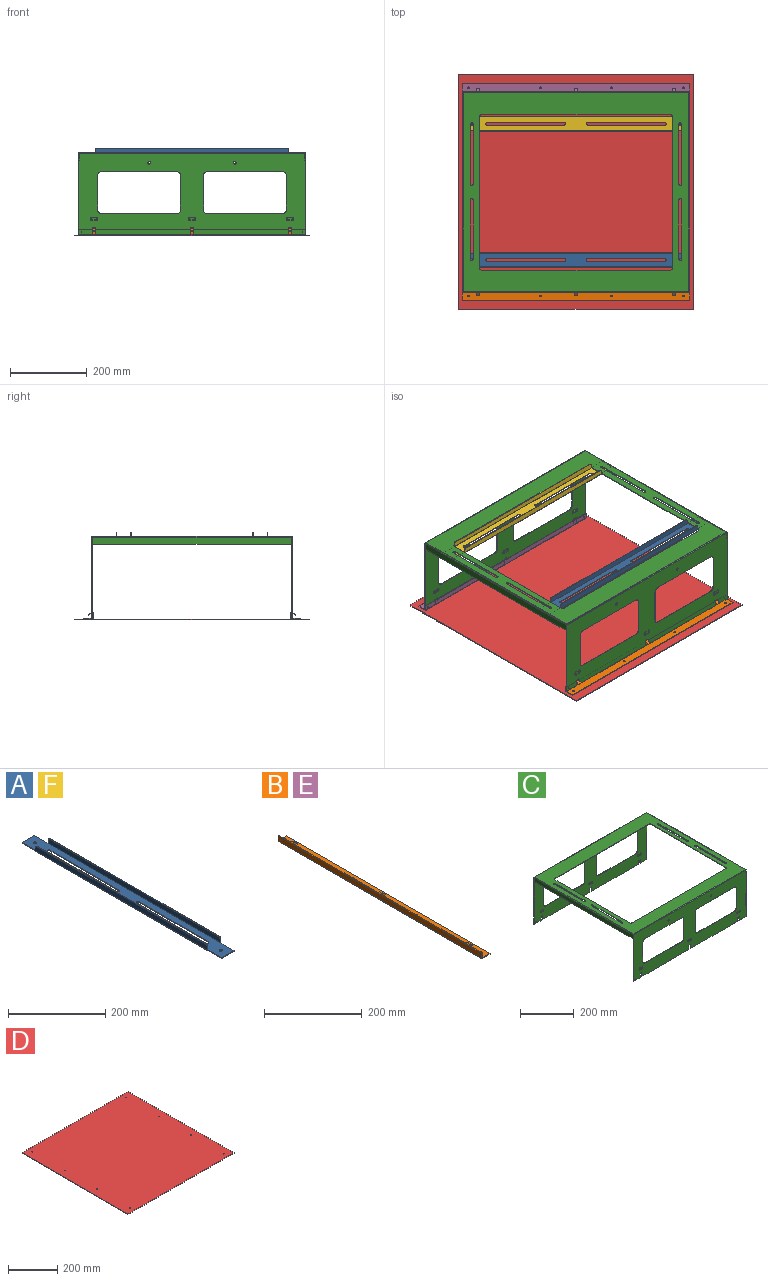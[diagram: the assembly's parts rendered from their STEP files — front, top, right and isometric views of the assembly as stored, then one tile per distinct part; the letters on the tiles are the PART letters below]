
ASSEMBLY  parts=6 mates=5
PART A: 40 faces, bbox 40x582x15 mm
  f0: plane 40x2mm, normal (-1,0,0), area 80mm2, adj f4,f16,f17,f36
  f1: plane 40x2mm, normal (1,0,0), area 80mm2, adj f2,f16,f17,f25
  f2: plane 35.8x2mm, normal (0,1,0), area 71.6mm2, adj f1,f15,f16,f17
  f3: plane 40x2mm, normal (1,0,0), area 80mm2, adj f4,f16,f17,f26
  f4: plane 35.8x2mm, normal (0,-1,0), area 71.6mm2, adj f0,f3,f16,f17
  f5: plane 200.9x2mm, normal (-1,0,0), area 401.8mm2, adj f6,f14,f16,f17
  f6: cylinder r=3.5mm len=7mm, axis (0,0,1), area 22.5mm2, adj f5,f7,f16,f17
  f7: plane 200.85x2mm, normal (1,0,0), area 401.7mm2, adj f6,f14,f16,f17
  f8: cylinder r=3.5mm len=7mm, axis (0,0,1), area 22mm2, adj f9,f11,f16,f17
  f9: plane 200.85x2mm, normal (1,0,0), area 401.7mm2, adj f8,f10,f16,f17
  f10: cylinder r=3.5mm len=7mm, axis (0,0,1), area 22.5mm2, adj f9,f11,f16,f17
  f11: plane 200.9x2mm, normal (-1,0,0), area 401.8mm2, adj f8,f10,f16,f17
  f12: cylinder r=3.5mm len=7mm, axis (0,0,1), area 44mm2, adj f16,f17
  f13: cylinder r=3.5mm len=7mm, axis (0,0,1), area 44mm2, adj f16,f17
  f14: cylinder r=3.5mm len=7mm, axis (0,0,1), area 22mm2, adj f5,f7,f16,f17
  f15: plane 40x2mm, normal (-1,0,0), area 80mm2, adj f2,f16,f17,f37
  f16: plane 582x35.8mm, normal (0,0,-1), area 17868.6mm2, adj f0,f1,f2,f3,f4,f5,f6,f7
  f17: plane 582x35.8mm, normal (0,0,1), area 17868.6mm2, adj f0,f1,f2,f3,f4,f5,f6,f7
  f18: plane 7.9x2mm, normal (0,-1,0), area 15.8mm2, adj f22,f23,f24,f26
  f19: plane 7.9x2mm, normal (0,1,0), area 15.8mm2, adj f20,f23,f24,f25
  f20: cylinder r=5mm len=5mm, axis (1,0,0), area 15.7mm2, adj f19,f21,f23,f24
  f21: plane 492x2mm, normal (0,0,1), area 984mm2, adj f20,f22,f23,f24
  f22: cylinder r=5mm len=5mm, axis (1,0,0), area 15.7mm2, adj f18,f21,f23,f24
  f23: plane 502x12.9mm, normal (1,0,0), area 6465.1mm2, adj f18,f19,f20,f21,f22,f27
  f24: plane 502x12.9mm, normal (-1,0,0), area 6465.1mm2, adj f18,f19,f20,f21,f22,f28
  f25: plane 2.1x2.1mm, normal (0,1,0), area 3.5mm2, adj f1,f19,f27,f28
  f26: plane 2.1x2.1mm, normal (0,-1,0), area 3.5mm2, adj f3,f18,f27,f28
  f27: cylinder r=2.1mm len=502mm, axis (0,1,0), area 1655.9mm2, adj f16,f23,f25,f26
  f28: cylinder r=0.1mm len=502mm, axis (0,1,0), area 78.9mm2, adj f17,f24,f25,f26
  f29: plane 492x2mm, normal (0,0,1), area 984mm2, adj f30,f33,f34,f35
  f30: cylinder r=5mm len=5mm, axis (-1,0,0), area 15.7mm2, adj f29,f31,f34,f35
  f31: plane 7.9x2mm, normal (0,1,0), area 15.8mm2, adj f30,f34,f35,f37
  f32: plane 7.9x2mm, normal (0,-1,0), area 15.8mm2, adj f33,f34,f35,f36
  f33: cylinder r=5mm len=5mm, axis (-1,0,0), area 15.7mm2, adj f29,f32,f34,f35
  f34: plane 502x12.9mm, normal (-1,0,0), area 6465.1mm2, adj f29,f30,f31,f32,f33,f38
  f35: plane 502x12.9mm, normal (1,0,0), area 6465.1mm2, adj f29,f30,f31,f32,f33,f39
  f36: plane 2.1x2.1mm, normal (0,-1,0), area 3.5mm2, adj f0,f32,f38,f39
  f37: plane 2.1x2.1mm, normal (0,1,0), area 3.5mm2, adj f15,f31,f38,f39
  f38: cylinder r=2.1mm len=502mm, axis (0,-1,0), area 1655.9mm2, adj f16,f34,f36,f37
  f39: cylinder r=0.1mm len=502mm, axis (0,-1,0), area 78.9mm2, adj f17,f35,f36,f37
PART B: 68 faces, bbox 25x590x17.9 mm
  f0: plane 22.9x2mm, normal (0,1,0), area 45.8mm2, adj f1,f7,f8,f65
  f1: plane 590x2mm, normal (1,0,0), area 1180mm2, adj f0,f2,f7,f8
  f2: plane 22.9x2mm, normal (0,-1,0), area 45.8mm2, adj f1,f7,f8,f64
  f3: cylinder r=2.25mm len=4.5mm, axis (0,0,1), area 28.3mm2, adj f7,f8
  f4: cylinder r=2.25mm len=4.5mm, axis (0,0,1), area 28.3mm2, adj f7,f8
  f5: cylinder r=2.25mm len=4.5mm, axis (0,0,1), area 28.3mm2, adj f7,f8
  f6: cylinder r=2.25mm len=4.5mm, axis (0,0,1), area 28.3mm2, adj f7,f8
  f7: plane 590x22.9mm, normal (0,0,-1), area 13447.4mm2, adj f0,f1,f2,f3,f4,f5,f6,f66
  f8: plane 590x22.9mm, normal (0,0,1), area 13447.4mm2, adj f0,f1,f2,f3,f4,f5,f6,f67
  f9: plane 2x0.27mm, normal (0,0,1), area 0.5mm2, adj f19,f20,f23,f36
  f10: plane 34.15x2mm, normal (0,0,1), area 68.3mm2, adj f19,f20,f22,f36
  f11: plane 2x0.27mm, normal (0,0,1), area 0.5mm2, adj f19,f20,f24,f35
  f12: plane 243.29x2mm, normal (0,0,1), area 486.6mm2, adj f19,f20,f34,f35
  f13: plane 2x0.27mm, normal (0,0,1), area 0.5mm2, adj f19,f20,f25,f34
  f14: plane 2x0.27mm, normal (0,0,1), area 0.5mm2, adj f19,f20,f26,f33
  f15: plane 243.29x2mm, normal (0,0,1), area 486.6mm2, adj f19,f20,f32,f33
  f16: plane 2x0.27mm, normal (0,0,1), area 0.5mm2, adj f19,f20,f27,f32
  f17: plane 2x0.27mm, normal (0,0,1), area 0.5mm2, adj f19,f20,f28,f31
  f18: plane 34.15x2mm, normal (0,0,1), area 68.3mm2, adj f19,f20,f21,f31
  f19: plane 590x13.71mm, normal (-1,0,0), area 7621.8mm2, adj f9,f10,f11,f12,f13,f14,f15,f16
  f20: plane 590x13.71mm, normal (1,0,0), area 7621.8mm2, adj f9,f10,f11,f12,f13,f14,f15,f16
  f21: plane 12.9x2mm, normal (0,1,0), area 25.8mm2, adj f18,f19,f20,f65
  f22: plane 12.9x2mm, normal (0,-1,0), area 25.8mm2, adj f10,f19,f20,f64
  f23: plane 2x0.81mm, normal (0,-1,0), area 1.6mm2, adj f9,f19,f20,f60
  f24: plane 2x0.81mm, normal (0,1,0), area 1.6mm2, adj f11,f19,f20,f61
  f25: plane 2x0.81mm, normal (0,-1,0), area 1.6mm2, adj f13,f19,f20,f43
  f26: plane 2x0.81mm, normal (0,1,0), area 1.6mm2, adj f14,f19,f20,f42
  f27: plane 2x0.81mm, normal (0,-1,0), area 1.6mm2, adj f16,f19,f20,f52
  f28: plane 2x0.81mm, normal (0,1,0), area 1.6mm2, adj f17,f19,f20,f51
  f29: cylinder r=1mm len=2mm, axis (-1,0,0), area 12.6mm2, adj f19,f20
  f30: cylinder r=1mm len=2mm, axis (-1,0,0), area 12.6mm2, adj f19,f20
  f31: cylinder r=1.06mm len=2mm, axis (1,0,0), area 3.6mm2, adj f17,f18,f19,f20
  f32: cylinder r=1.06mm len=2mm, axis (1,0,0), area 3.6mm2, adj f15,f16,f19,f20
  f33: cylinder r=1.06mm len=2mm, axis (1,0,0), area 3.6mm2, adj f14,f15,f19,f20
  f34: cylinder r=1.06mm len=2mm, axis (1,0,0), area 3.6mm2, adj f12,f13,f19,f20
  f35: cylinder r=1.06mm len=2mm, axis (1,0,0), area 3.6mm2, adj f11,f12,f19,f20
  f36: cylinder r=1.06mm len=2mm, axis (1,0,0), area 3.6mm2, adj f9,f10,f19,f20
  f37: plane 8x1.64mm, normal (0.82,0,-0.57), area 16mm2, adj f38,f39,f40,f41
  f38: plane 10.13x7.93mm, normal (0,1,0), area 21.9mm2, adj f37,f40,f41,f42
  f39: plane 10.13x7.93mm, normal (0,-1,0), area 21.9mm2, adj f37,f40,f41,f43
  f40: plane 8.98x8mm, normal (0.57,0,0.82), area 87.7mm2, adj f37,f38,f39,f44
  f41: plane 8.98x8mm, normal (-0.57,0,-0.82), area 87.7mm2, adj f37,f38,f39,f45
  f42: plane 3.3x2.1mm, normal (0,1,0), area 4.8mm2, adj f26,f38,f44,f45
  f43: plane 3.3x2.1mm, normal (0,-1,0), area 4.8mm2, adj f25,f39,f44,f45
  f44: cylinder r=2.1mm len=8mm, axis (0,1,0), area 36.7mm2, adj f19,f40,f42,f43
  f45: cylinder r=0.1mm len=8mm, axis (0,1,0), area 1.7mm2, adj f20,f41,f42,f43
  f46: plane 8x1.64mm, normal (0.82,0,-0.57), area 16mm2, adj f47,f48,f49,f50
  f47: plane 10.13x7.93mm, normal (0,1,0), area 21.9mm2, adj f46,f49,f50,f51
  f48: plane 10.13x7.93mm, normal (0,-1,0), area 21.9mm2, adj f46,f49,f50,f52
  f49: plane 8.98x8mm, normal (0.57,0,0.82), area 87.7mm2, adj f46,f47,f48,f53
  f50: plane 8.98x8mm, normal (-0.57,0,-0.82), area 87.7mm2, adj f46,f47,f48,f54
  f51: plane 3.3x2.1mm, normal (0,1,0), area 4.8mm2, adj f28,f47,f53,f54
  f52: plane 3.3x2.1mm, normal (0,-1,0), area 4.8mm2, adj f27,f48,f53,f54
  f53: cylinder r=2.1mm len=8mm, axis (0,1,0), area 36.7mm2, adj f19,f49,f51,f52
  f54: cylinder r=0.1mm len=8mm, axis (0,1,0), area 1.7mm2, adj f20,f50,f51,f52
  f55: plane 8x1.64mm, normal (0.82,0,-0.57), area 16mm2, adj f56,f57,f58,f59
  f56: plane 10.13x7.93mm, normal (0,1,0), area 21.9mm2, adj f55,f58,f59,f61
  f57: plane 10.13x7.93mm, normal (0,-1,0), area 21.9mm2, adj f55,f58,f59,f60
  f58: plane 8.98x8mm, normal (0.57,0,0.82), area 87.7mm2, adj f55,f56,f57,f62
  f59: plane 8.98x8mm, normal (-0.57,0,-0.82), area 87.7mm2, adj f55,f56,f57,f63
  f60: plane 3.3x2.1mm, normal (0,-1,0), area 4.8mm2, adj f23,f57,f62,f63
  f61: plane 3.3x2.1mm, normal (0,1,0), area 4.8mm2, adj f24,f56,f62,f63
  f62: cylinder r=2.1mm len=8mm, axis (0,-1,0), area 36.7mm2, adj f19,f58,f60,f61
  f63: cylinder r=0.1mm len=8mm, axis (0,-1,0), area 1.7mm2, adj f20,f59,f60,f61
  f64: plane 2.1x2.1mm, normal (0,-1,0), area 3.5mm2, adj f2,f22,f66,f67
  f65: plane 2.1x2.1mm, normal (0,1,0), area 3.5mm2, adj f0,f21,f66,f67
  f66: cylinder r=2.1mm len=590mm, axis (0,-1,0), area 1946.2mm2, adj f7,f19,f64,f65
  f67: cylinder r=0.1mm len=590mm, axis (0,-1,0), area 92.7mm2, adj f8,f20,f64,f65
PART C: 200 faces, bbox 590x521x213 mm
  f0: cylinder r=3.5mm len=7mm, axis (0,0,1), area 22mm2, adj f1,f23,f24,f25
  f1: plane 155x2mm, normal (-1,0,0), area 310mm2, adj f0,f2,f24,f25
  f2: cylinder r=3.5mm len=7mm, axis (0,0,1), area 22mm2, adj f1,f23,f24,f25
  f3: plane 390x2mm, normal (1,0,0), area 780mm2, adj f4,f22,f24,f25
  f4: cylinder r=7mm len=7mm, axis (0,0,1), area 22mm2, adj f3,f5,f24,f25
  f5: plane 490x2mm, normal (0,1,0), area 980mm2, adj f4,f6,f24,f25
  f6: cylinder r=7mm len=7mm, axis (0,0,1), area 22mm2, adj f5,f7,f24,f25
  f7: plane 390x2mm, normal (-1,0,0), area 780mm2, adj f6,f8,f24,f25
  f8: cylinder r=7mm len=7mm, axis (0,0,1), area 22mm2, adj f7,f9,f24,f25
  f9: plane 490x2mm, normal (0,-1,0), area 980mm2, adj f8,f22,f24,f25
  f10: plane 155x2mm, normal (1,0,0), area 310mm2, adj f11,f21,f24,f25
  f11: cylinder r=3.5mm len=7mm, axis (0,0,1), area 22mm2, adj f10,f12,f24,f25
  f12: plane 155x2mm, normal (-1,0,0), area 310mm2, adj f11,f21,f24,f25
  f13: cylinder r=3.5mm len=7mm, axis (0,0,1), area 22mm2, adj f14,f20,f24,f25
  f14: plane 155x2mm, normal (1,0,0), area 310mm2, adj f13,f15,f24,f25
  f15: cylinder r=3.5mm len=7mm, axis (0,0,1), area 22mm2, adj f14,f20,f24,f25
  f16: cylinder r=3.5mm len=7mm, axis (0,0,1), area 22mm2, adj f17,f19,f24,f25
  f17: plane 155x2mm, normal (-1,0,0), area 310mm2, adj f16,f18,f24,f25
  f18: cylinder r=3.5mm len=7mm, axis (0,0,1), area 22mm2, adj f17,f19,f24,f25
  f19: plane 155x2mm, normal (1,0,0), area 310mm2, adj f16,f18,f24,f25
  f20: plane 155x2mm, normal (-1,0,0), area 310mm2, adj f13,f15,f24,f25
  f21: cylinder r=3.5mm len=7mm, axis (0,0,1), area 22mm2, adj f10,f12,f24,f25
  f22: cylinder r=7mm len=7mm, axis (0,0,1), area 22mm2, adj f3,f9,f24,f25
  f23: plane 155x2mm, normal (1,0,0), area 310mm2, adj f0,f2,f24,f25
  f24: plane 585.8x516.8mm, normal (0,0,-1), area 94673.6mm2, adj f0,f1,f2,f3,f4,f5,f6,f7
  f25: plane 585.8x516.8mm, normal (0,0,1), area 94673.6mm2, adj f0,f1,f2,f3,f4,f5,f6,f7
  f26: plane 2.1x2mm, normal (0,0,1), area 4.2mm2, adj f40,f98,f99,f101
  f27: plane 9x2mm, normal (0,0,-1), area 18mm2, adj f28,f97,f98,f99
  f28: plane 17x2mm, normal (1,0,0), area 34mm2, adj f27,f29,f98,f99
  f29: plane 246.17x2mm, normal (0,0,-1), area 492.3mm2, adj f28,f30,f98,f99
  f30: plane 17x2mm, normal (-1,0,0), area 34mm2, adj f29,f31,f98,f99
  f31: plane 9x2mm, normal (0,0,-1), area 18mm2, adj f30,f32,f98,f99
  f32: plane 17x2mm, normal (1,0,0), area 34mm2, adj f31,f33,f98,f99
  f33: plane 246x2mm, normal (0,0,-1), area 492mm2, adj f32,f34,f98,f99
  f34: plane 17x2mm, normal (-1,0,0), area 34mm2, adj f33,f35,f98,f99
  f35: plane 9x2mm, normal (0,0,-1), area 18mm2, adj f34,f36,f98,f99
  f36: plane 17x2mm, normal (1,0,0), area 34mm2, adj f35,f37,f98,f99
  f37: plane 35.5x2mm, normal (0,0,-1), area 71mm2, adj f36,f38,f98,f99
  f38: plane 210.9x2mm, normal (-1,0,0), area 421.8mm2, adj f37,f39,f98,f99
  f39: plane 2.1x2mm, normal (0,0,1), area 4.2mm2, adj f38,f98,f99,f100
  f40: plane 210.9x2mm, normal (1,0,0), area 421.8mm2, adj f26,f41,f98,f99
  f41: plane 35.33x2mm, normal (0,0,-1), area 70.7mm2, adj f40,f97,f98,f99
  f42: plane 195x2mm, normal (0,0,-1), area 390mm2, adj f43,f96,f98,f99
  f43: cylinder r=10mm len=10mm, axis (0,1,0), area 31.4mm2, adj f42,f44,f98,f99
  f44: plane 90x2mm, normal (1,0,0), area 180mm2, adj f43,f45,f98,f99
  f45: cylinder r=10mm len=10mm, axis (0,1,0), area 31.4mm2, adj f44,f46,f98,f99
  f46: plane 195x2mm, normal (0,0,1), area 390mm2, adj f45,f47,f98,f99
  f47: cylinder r=10mm len=10mm, axis (0,1,0), area 31.4mm2, adj f46,f48,f98,f99
  f48: plane 90x2mm, normal (-1,0,0), area 180mm2, adj f47,f96,f98,f99
  f49: cylinder r=10mm len=10mm, axis (0,1,0), area 31.4mm2, adj f50,f95,f98,f99
  f50: plane 195x2mm, normal (0,0,-1), area 390mm2, adj f49,f51,f98,f99
  f51: cylinder r=10mm len=10mm, axis (0,1,0), area 31.4mm2, adj f50,f52,f98,f99
  f52: plane 90x2mm, normal (1,0,0), area 180mm2, adj f51,f53,f98,f99
  f53: cylinder r=10mm len=10mm, axis (0,1,0), area 31.4mm2, adj f52,f54,f98,f99
  f54: plane 195x2mm, normal (0,0,1), area 390mm2, adj f53,f55,f98,f99
  f55: cylinder r=10mm len=10mm, axis (0,1,0), area 31.4mm2, adj f54,f95,f98,f99
  f56: cylinder r=5mm len=10mm, axis (0,1,0), area 31.5mm2, adj f57,f94,f98,f99
  f57: plane 2.5x2mm, normal (0,0,1), area 5mm2, adj f56,f58,f98,f99
  f58: plane 2.5x2mm, normal (-1,0,0), area 5mm2, adj f57,f59,f98,f99
  f59: plane 2.5x2mm, normal (0,0,-1), area 5mm2, adj f58,f60,f98,f99
  f60: cylinder r=2.5mm len=4.93mm, axis (0,1,0), area 14.5mm2, adj f59,f61,f98,f99
  f61: plane 10.56x2mm, normal (-0.01,0,1), area 21.1mm2, adj f60,f62,f98,f99
  f62: cylinder r=2.5mm len=5mm, axis (0,1,0), area 15.7mm2, adj f61,f63,f98,f99
  f63: plane 2.5x2mm, normal (0,0,-1), area 5mm2, adj f62,f64,f98,f99
  f64: plane 2.5x2mm, normal (1,0,0), area 5mm2, adj f63,f65,f98,f99
  f65: plane 2.5x2mm, normal (0,0,1), area 5mm2, adj f64,f66,f98,f99
  f66: cylinder r=5mm len=10mm, axis (0,1,0), area 31.4mm2, adj f65,f94,f98,f99
  f67: plane 9.97x2mm, normal (0,0,-1), area 19.9mm2, adj f68,f93,f98,f99
  f68: cylinder r=5mm len=10mm, axis (0,1,0), area 31.4mm2, adj f67,f69,f98,f99
  f69: plane 2.5x2mm, normal (0,0,1), area 5mm2, adj f68,f70,f98,f99
  f70: plane 2.5x2mm, normal (-1,0,0), area 5mm2, adj f69,f71,f98,f99
  f71: plane 2.5x2mm, normal (0,0,-1), area 5mm2, adj f70,f72,f98,f99
  f72: cylinder r=2.5mm len=5mm, axis (0,1,0), area 15.7mm2, adj f71,f73,f98,f99
  f73: plane 10.56x2mm, normal (0.01,0,1), area 21.1mm2, adj f72,f74,f98,f99
  f74: cylinder r=2.5mm len=4.93mm, axis (0,1,0), area 14.5mm2, adj f73,f75,f98,f99
  f75: plane 2.5x2mm, normal (0,0,-1), area 5mm2, adj f74,f76,f98,f99
  f76: plane 2.5x2mm, normal (1,0,0), area 5mm2, adj f75,f77,f98,f99
  f77: plane 2.5x2mm, normal (0,0,1), area 5mm2, adj f76,f93,f98,f99
  f78: plane 2.5x2mm, normal (0,0,1), area 5mm2, adj f79,f90,f98,f99
  f79: cylinder r=5mm len=10mm, axis (0,1,0), area 31.5mm2, adj f78,f80,f98,f99
  f80: plane 9.97x2mm, normal (0,0,-1), area 19.9mm2, adj f79,f81,f98,f99
  f81: cylinder r=5mm len=10mm, axis (0,1,0), area 31.4mm2, adj f80,f82,f98,f99
  f82: plane 2.5x2mm, normal (0,0,1), area 5mm2, adj f81,f83,f98,f99
  f83: plane 2.5x2mm, normal (-1,0,0), area 5mm2, adj f82,f84,f98,f99
  f84: plane 2.5x2mm, normal (0,0,-1), area 5mm2, adj f83,f85,f98,f99
  f85: cylinder r=2.5mm len=5mm, axis (0,1,0), area 15.7mm2, adj f84,f86,f98,f99
  f86: plane 10.56x2mm, normal (0.01,0,1), area 21.1mm2, adj f85,f87,f98,f99
  f87: cylinder r=2.5mm len=4.93mm, axis (0,1,0), area 14.5mm2, adj f86,f88,f98,f99
  f88: plane 2.5x2mm, normal (0,0,-1), area 5mm2, adj f87,f90,f98,f99
  f89: cylinder r=3.5mm len=7mm, axis (0,1,0), area 44mm2, adj f98,f99
  f90: plane 2.5x2mm, normal (1,0,0), area 5mm2, adj f78,f88,f98,f99
  f91: cylinder r=1mm len=2mm, axis (0,1,0), area 12.6mm2, adj f98,f99
  f92: cylinder r=3.5mm len=7mm, axis (0,1,0), area 44mm2, adj f98,f99
  f93: cylinder r=5mm len=10mm, axis (0,1,0), area 31.5mm2, adj f67,f77,f98,f99
  f94: plane 9.97x2mm, normal (0,0,-1), area 19.9mm2, adj f56,f66,f98,f99
  f95: plane 90x2mm, normal (-1,0,0), area 180mm2, adj f49,f55,f98,f99
  f96: cylinder r=10mm len=10mm, axis (0,1,0), area 31.4mm2, adj f42,f48,f98,f99
  f97: plane 17x2mm, normal (-1,0,0), area 34mm2, adj f27,f41,f98,f99
  f98: plane 590x210.9mm, normal (0,1,0), area 76473.3mm2, adj f26,f27,f28,f29,f30,f31,f32,f33
  f99: plane 590x210.9mm, normal (0,-1,0), area 76473.3mm2, adj f26,f27,f28,f29,f30,f31,f32,f33
  f100: plane 2.1x2.1mm, normal (-1,0,0), area 3.5mm2, adj f39,f102,f103,f197
  f101: plane 2.1x2.1mm, normal (1,0,0), area 3.5mm2, adj f26,f102,f103,f187
  f102: cylinder r=2.1mm len=585.8mm, axis (-1,0,0), area 1932.4mm2, adj f25,f99,f100,f101
  f103: cylinder r=0.1mm len=585.8mm, axis (-1,0,0), area 92mm2, adj f24,f98,f100,f101
  f104: plane 2.1x2mm, normal (0,0,1), area 4.2mm2, adj f118,f176,f177,f178
  f105: plane 9x2mm, normal (0,0,-1), area 18mm2, adj f106,f175,f176,f177
  f106: plane 17x2mm, normal (-1,0,0), area 34mm2, adj f105,f107,f176,f177
  f107: plane 246x2mm, normal (0,0,-1), area 492mm2, adj f106,f108,f176,f177
  f108: plane 17x2mm, normal (1,0,0), area 34mm2, adj f107,f109,f176,f177
  f109: plane 9x2mm, normal (0,0,-1), area 18mm2, adj f108,f110,f176,f177
  f110: plane 17x2mm, normal (-1,0,0), area 34mm2, adj f109,f111,f176,f177
  f111: plane 246.17x2mm, normal (0,0,-1), area 492.3mm2, adj f110,f112,f176,f177
  f112: plane 17x2mm, normal (1,0,0), area 34mm2, adj f111,f113,f176,f177
  f113: plane 9x2mm, normal (0,0,-1), area 18mm2, adj f112,f114,f176,f177
  f114: plane 17x2mm, normal (-1,0,0), area 34mm2, adj f113,f115,f176,f177
  f115: plane 35.33x2mm, normal (0,0,-1), area 70.7mm2, adj f114,f116,f176,f177
  f116: plane 210.9x2mm, normal (1,0,0), area 421.8mm2, adj f115,f117,f176,f177
  f117: plane 2.1x2mm, normal (0,0,1), area 4.2mm2, adj f116,f176,f177,f179
  f118: plane 210.9x2mm, normal (-1,0,0), area 421.8mm2, adj f104,f119,f176,f177
  f119: plane 35.5x2mm, normal (0,0,-1), area 71mm2, adj f118,f175,f176,f177
  f120: plane 90x2mm, normal (-1,0,0), area 180mm2, adj f121,f174,f176,f177
  f121: cylinder r=10mm len=10mm, axis (0,-1,0), area 31.4mm2, adj f120,f122,f176,f177
  f122: plane 195x2mm, normal (0,0,1), area 390mm2, adj f121,f123,f176,f177
  f123: cylinder r=10mm len=10mm, axis (0,-1,0), area 31.4mm2, adj f122,f124,f176,f177
  f124: plane 90x2mm, normal (1,0,0), area 180mm2, adj f123,f125,f176,f177
  f125: cylinder r=10mm len=10mm, axis (0,-1,0), area 31.4mm2, adj f124,f126,f176,f177
  f126: plane 195x2mm, normal (0,0,-1), area 390mm2, adj f125,f174,f176,f177
  f127: cylinder r=10mm len=10mm, axis (0,-1,0), area 31.4mm2, adj f128,f173,f176,f177
  f128: plane 195x2mm, normal (0,0,1), area 390mm2, adj f127,f129,f176,f177
  f129: cylinder r=10mm len=10mm, axis (0,-1,0), area 31.4mm2, adj f128,f130,f176,f177
  f130: plane 90x2mm, normal (1,0,0), area 180mm2, adj f129,f131,f176,f177
  f131: cylinder r=10mm len=10mm, axis (0,-1,0), area 31.4mm2, adj f130,f132,f176,f177
  f132: plane 195x2mm, normal (0,0,-1), area 390mm2, adj f131,f133,f176,f177
  f133: cylinder r=10mm len=10mm, axis (0,-1,0), area 31.4mm2, adj f132,f173,f176,f177
  f134: cylinder r=5mm len=10mm, axis (0,-1,0), area 31.4mm2, adj f135,f172,f176,f177
  f135: plane 2.5x2mm, normal (0,0,1), area 5mm2, adj f134,f136,f176,f177
  f136: plane 2.5x2mm, normal (1,0,0), area 5mm2, adj f135,f137,f176,f177
  f137: plane 2.5x2mm, normal (0,0,-1), area 5mm2, adj f136,f138,f176,f177
  f138: cylinder r=2.5mm len=5mm, axis (0,-1,0), area 15.7mm2, adj f137,f139,f176,f177
  f139: plane 10.56x2mm, normal (-0.01,0,1), area 21.1mm2, adj f138,f140,f176,f177
  f140: cylinder r=2.5mm len=4.93mm, axis (0,-1,0), area 14.5mm2, adj f139,f141,f176,f177
  f141: plane 2.5x2mm, normal (0,0,-1), area 5mm2, adj f140,f142,f176,f177
  f142: plane 2.5x2mm, normal (-1,0,0), area 5mm2, adj f141,f143,f176,f177
  f143: plane 2.5x2mm, normal (0,0,1), area 5mm2, adj f142,f144,f176,f177
  f144: cylinder r=5mm len=10mm, axis (0,-1,0), area 31.5mm2, adj f143,f172,f176,f177
  f145: plane 2.5x2mm, normal (0,0,1), area 5mm2, adj f146,f171,f176,f177
  f146: plane 2.5x2mm, normal (1,0,0), area 5mm2, adj f145,f147,f176,f177
  f147: plane 2.5x2mm, normal (0,0,-1), area 5mm2, adj f146,f148,f176,f177
  f148: cylinder r=2.5mm len=4.93mm, axis (0,-1,0), area 14.5mm2, adj f147,f149,f176,f177
  f149: plane 10.56x2mm, normal (0.01,0,1), area 21.1mm2, adj f148,f150,f176,f177
  f150: cylinder r=2.5mm len=5mm, axis (0,-1,0), area 15.7mm2, adj f149,f151,f176,f177
  f151: plane 2.5x2mm, normal (0,0,-1), area 5mm2, adj f150,f152,f176,f177
  f152: plane 2.5x2mm, normal (-1,0,0), area 5mm2, adj f151,f153,f176,f177
  f153: plane 2.5x2mm, normal (0,0,1), area 5mm2, adj f152,f154,f176,f177
  f154: cylinder r=5mm len=10mm, axis (0,-1,0), area 31.4mm2, adj f153,f155,f176,f177
  f155: plane 9.97x2mm, normal (0,0,-1), area 19.9mm2, adj f154,f171,f176,f177
  f156: plane 10.56x2mm, normal (0.01,0,1), area 21.1mm2, adj f157,f168,f176,f177
  f157: cylinder r=2.5mm len=5mm, axis (0,-1,0), area 15.7mm2, adj f156,f158,f176,f177
  f158: plane 2.5x2mm, normal (0,0,-1), area 5mm2, adj f157,f159,f176,f177
  f159: plane 2.5x2mm, normal (-1,0,0), area 5mm2, adj f158,f160,f176,f177
  f160: plane 2.5x2mm, normal (0,0,1), area 5mm2, adj f159,f161,f176,f177
  f161: cylinder r=5mm len=10mm, axis (0,-1,0), area 31.4mm2, adj f160,f162,f176,f177
  f162: plane 9.97x2mm, normal (0,0,-1), area 19.9mm2, adj f161,f163,f176,f177
  f163: cylinder r=5mm len=10mm, axis (0,-1,0), area 31.5mm2, adj f162,f164,f176,f177
  f164: plane 2.5x2mm, normal (0,0,1), area 5mm2, adj f163,f165,f176,f177
  f165: plane 2.5x2mm, normal (1,0,0), area 5mm2, adj f164,f166,f176,f177
  f166: plane 2.5x2mm, normal (0,0,-1), area 5mm2, adj f165,f168,f176,f177
  f167: cylinder r=3.5mm len=7mm, axis (0,-1,0), area 44mm2, adj f176,f177
  f168: cylinder r=2.5mm len=4.93mm, axis (0,-1,0), area 14.5mm2, adj f156,f166,f176,f177
  f169: cylinder r=1mm len=2mm, axis (0,-1,0), area 12.6mm2, adj f176,f177
  f170: cylinder r=3.5mm len=7mm, axis (0,-1,0), area 44mm2, adj f176,f177
  f171: cylinder r=5mm len=10mm, axis (0,-1,0), area 31.5mm2, adj f145,f155,f176,f177
  f172: plane 9.97x2mm, normal (0,0,-1), area 19.9mm2, adj f134,f144,f176,f177
  f173: plane 90x2mm, normal (-1,0,0), area 180mm2, adj f127,f133,f176,f177
  f174: cylinder r=10mm len=10mm, axis (0,-1,0), area 31.4mm2, adj f120,f126,f176,f177
  f175: plane 17x2mm, normal (1,0,0), area 34mm2, adj f105,f119,f176,f177
  f176: plane 590x210.9mm, normal (0,-1,0), area 76473.3mm2, adj f104,f105,f106,f107,f108,f109,f110,f111
  f177: plane 590x210.9mm, normal (0,1,0), area 76473.3mm2, adj f104,f105,f106,f107,f108,f109,f110,f111
  f178: plane 2.1x2.1mm, normal (-1,0,0), area 3.5mm2, adj f104,f180,f181,f196
  f179: plane 2.1x2.1mm, normal (1,0,0), area 3.5mm2, adj f117,f180,f181,f188
  f180: cylinder r=2.1mm len=585.8mm, axis (-1,0,0), area 1932.4mm2, adj f25,f177,f178,f179
  f181: cylinder r=0.1mm len=585.8mm, axis (-1,0,0), area 92mm2, adj f24,f176,f178,f179
  f182: plane 516.8x2mm, normal (0,0,-1), area 1033.6mm2, adj f183,f184,f185,f186
  f183: plane 17.9x2mm, normal (0,-1,0), area 35.8mm2, adj f182,f185,f186,f187
  f184: plane 17.9x2mm, normal (0,1,0), area 35.8mm2, adj f182,f185,f186,f188
  f185: plane 516.8x17.9mm, normal (-1,0,0), area 9250.7mm2, adj f182,f183,f184,f190
  f186: plane 516.8x17.9mm, normal (1,0,0), area 9250.7mm2, adj f182,f183,f184,f189
  f187: plane 2.1x2.1mm, normal (0,-1,0), area 3.5mm2, adj f101,f183,f189,f190
  f188: plane 2.1x2.1mm, normal (0,1,0), area 3.5mm2, adj f179,f184,f189,f190
  f189: cylinder r=2.1mm len=516.8mm, axis (0,-1,0), area 1704.8mm2, adj f25,f186,f187,f188
  f190: cylinder r=0.1mm len=516.8mm, axis (0,-1,0), area 81.2mm2, adj f24,f185,f187,f188
  f191: plane 516.8x2mm, normal (0,0,-1), area 1033.6mm2, adj f192,f193,f194,f195
  f192: plane 17.9x2mm, normal (0,1,0), area 35.8mm2, adj f191,f194,f195,f196
  f193: plane 17.9x2mm, normal (0,-1,0), area 35.8mm2, adj f191,f194,f195,f197
  f194: plane 516.8x17.9mm, normal (1,0,0), area 9250.7mm2, adj f191,f192,f193,f199
  f195: plane 516.8x17.9mm, normal (-1,0,0), area 9250.7mm2, adj f191,f192,f193,f198
  f196: plane 2.1x2.1mm, normal (0,1,0), area 3.5mm2, adj f178,f192,f198,f199
  f197: plane 2.1x2.1mm, normal (0,-1,0), area 3.5mm2, adj f100,f193,f198,f199
  f198: cylinder r=2.1mm len=516.8mm, axis (0,1,0), area 1704.8mm2, adj f25,f195,f196,f197
  f199: cylinder r=0.1mm len=516.8mm, axis (0,1,0), area 81.2mm2, adj f24,f194,f196,f197
PART D: 14 faces, bbox 610x610x2 mm
  f0: plane 610x2mm, normal (0,1,0), area 1220mm2, adj f1,f7,f12,f13
  f1: plane 610x2mm, normal (1,0,0), area 1220mm2, adj f0,f2,f12,f13
  f2: plane 610x2mm, normal (0,-1,0), area 1220mm2, adj f1,f7,f12,f13
  f3: cylinder r=2.25mm len=4.5mm, axis (0,0,1), area 28.3mm2, adj f12,f13
  f4: cylinder r=2.25mm len=4.5mm, axis (0,0,1), area 28.3mm2, adj f12,f13
  f5: cylinder r=2.25mm len=4.5mm, axis (0,0,1), area 28.3mm2, adj f12,f13
  f6: cylinder r=2.25mm len=4.5mm, axis (0,0,1), area 28.3mm2, adj f12,f13
  f7: plane 610x2mm, normal (-1,0,0), area 1220mm2, adj f0,f2,f12,f13
  f8: cylinder r=2.25mm len=4.5mm, axis (0,0,1), area 28.3mm2, adj f12,f13
  f9: cylinder r=2.25mm len=4.5mm, axis (0,0,1), area 28.3mm2, adj f12,f13
  f10: cylinder r=2.25mm len=4.5mm, axis (0,0,1), area 28.3mm2, adj f12,f13
  f11: cylinder r=2.25mm len=4.5mm, axis (0,0,1), area 28.3mm2, adj f12,f13
  f12: plane 610x610mm, normal (0,0,-1), area 371972.8mm2, adj f0,f1,f2,f3,f4,f5,f6,f7
  f13: plane 610x610mm, normal (0,0,1), area 371972.8mm2, adj f0,f1,f2,f3,f4,f5,f6,f7
PART E: same geometry as B
PART F: same geometry as A
PLACE A rot(axis=(0,0,-1),90deg) t=(-239.83,-378.33,-209.28)mm
PLACE B rot(axis=(0,0,-1),90deg) t=(-239.83,-470.83,-420.28)mm
PLACE C rot(axis=(0,0,1),0deg) t=(-239.83,-201.33,-207.28)mm
PLACE D rot(axis=(0,0,-1),90deg) t=(-239.83,-201.38,-422.28)mm
PLACE E rot(axis=(0,0,1),90deg) t=(-239.83,68.17,-420.28)mm
PLACE F rot(axis=(0,0,-1),90deg) t=(-239.83,-24.33,-209.28)mm
MATE parallel C.f91 <-> C.f91  axis (0,1,0) through (-526.83,-459.83,-412.28)mm
MATE parallel C.f16 <-> A.f12  axis (0,0,-1) through (-510.83,-376.83,-207.28)mm
MATE parallel E.f30 <-> C.f91  axis (0,1,0) through (-526.83,57.67,-412.28)mm
MATE parallel F.f12 <-> C.f21  axis (0,0,-1) through (-510.83,-24.33,-209.28)mm
MATE parallel F.f12 <-> C.f21  axis (0,0,1) through (-510.83,-24.33,-207.28)mm
